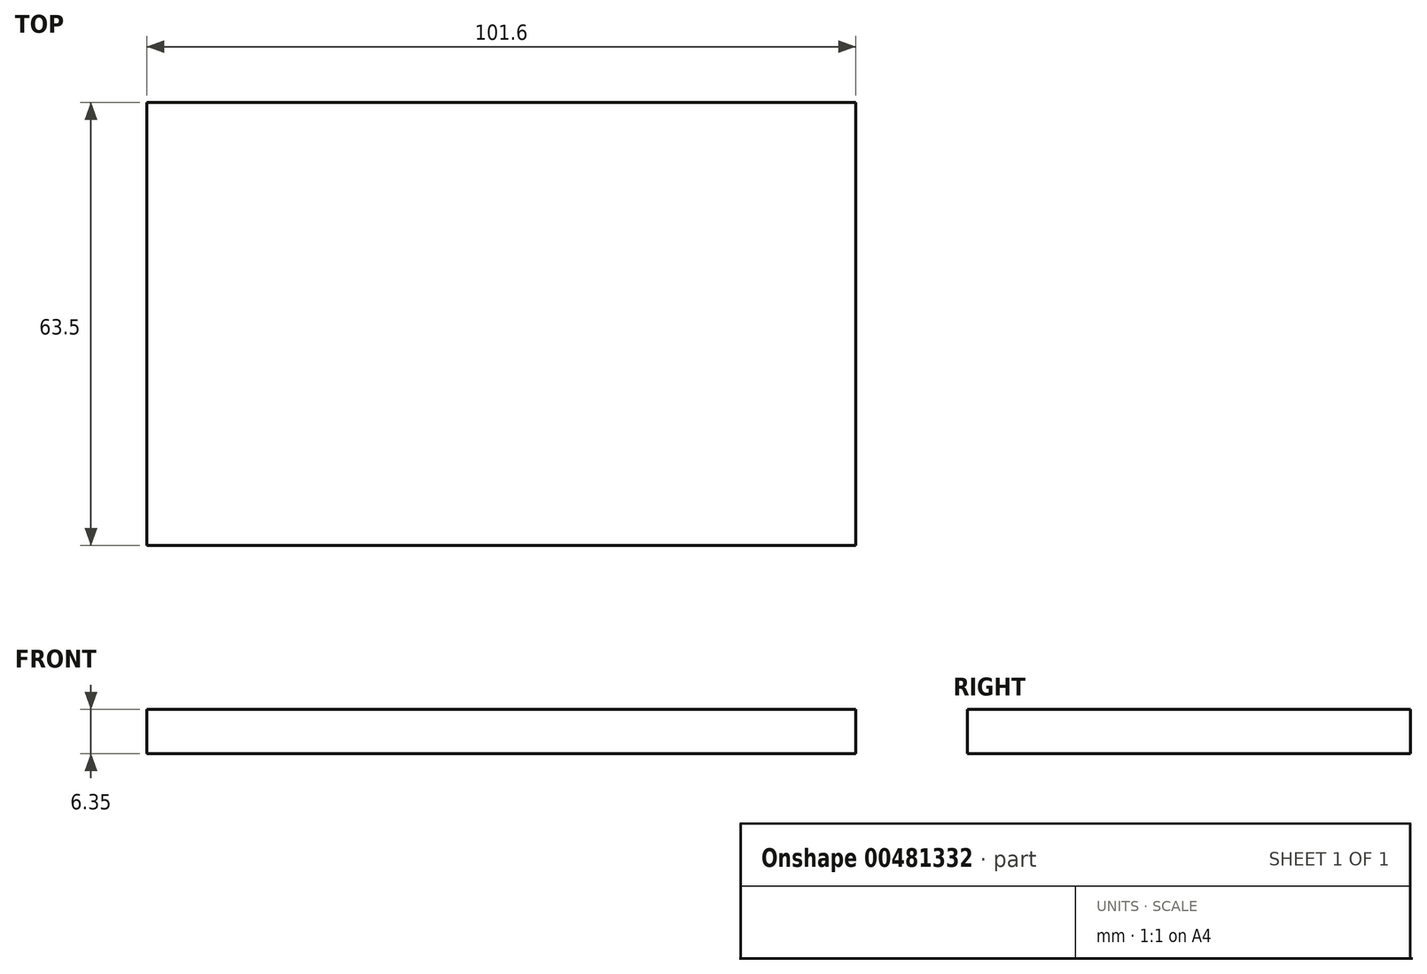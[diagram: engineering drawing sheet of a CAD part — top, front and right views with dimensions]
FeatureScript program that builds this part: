
annotation { "Feature Type Name" : "Feature", "Feature Type Description" : "" }
export const myFeature = defineFeature(function(context is Context, id is Id, definition is map)
    precondition{}
    {
        {
            var Q0;
            Q0=qCreatedBy(makeId("Front.planeOp"),FACE);
            var sketch = newSketch(context, id + "F0", { "sketchPlane" : qUnion([Q0])});
            skLineSegment(sketch, "E0.bottom", {"start": v(-46.86, 14.43) * mm, "end": v(54.74, 14.43) * mm});
            skLineSegment(sketch, "E0.top", {"start": v(-46.86, 8.08) * mm, "end": v(54.74, 8.08) * mm});
            skLineSegment(sketch, "E0.left", {"start": v(-46.86, 14.43) * mm, "end": v(-46.86, 8.08) * mm});
            skLineSegment(sketch, "E0.right", {"start": v(54.74, 14.43) * mm, "end": v(54.74, 8.08) * mm});
            skSolve(sketch);
        }
        {
            var Q0;
            Q0=makeQuery(id+"F0.imprint","IMPRINT",FACE,{"disambiguationData":[TD([[makeQuery(id+"F0.imprint","IMPRINT",EDGE,{"derivedFrom":sQuery(id+"F0.wireOp",EDGE,"E0.bottom")}),-1.0]])]});
            extrude(context, id + "F1", {"entities" : qUnion([Q0]), "depth" : 63.5 * mm});
        }
    });
